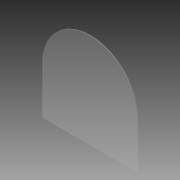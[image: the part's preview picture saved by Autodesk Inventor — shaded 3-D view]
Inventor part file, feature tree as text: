
AUTODESK INVENTOR PART (.ipt)
format: ipt  version: 2012 (Build 160160000, 160)  size: 68,608 bytes
history: native  units: in
note: dims shown in document units (in); Inventor stores cm internally (conversion verified against a paired STEP export)
features: extrude x1, sketch x1
ambient origin geometry x8: Origin, YZ Plane, XZ Plane, XY Plane, X Axis, Y Axis, Z Axis, Center Point
bodies: Solid1 (feature_tree)
feature tree (2):
  extrude  "Extrusion1"  Depth=12.0in
  sketch  "Sketch1"  dims[d0=6.0in d1=12.0in d2=0.125in d3=0.0in]
